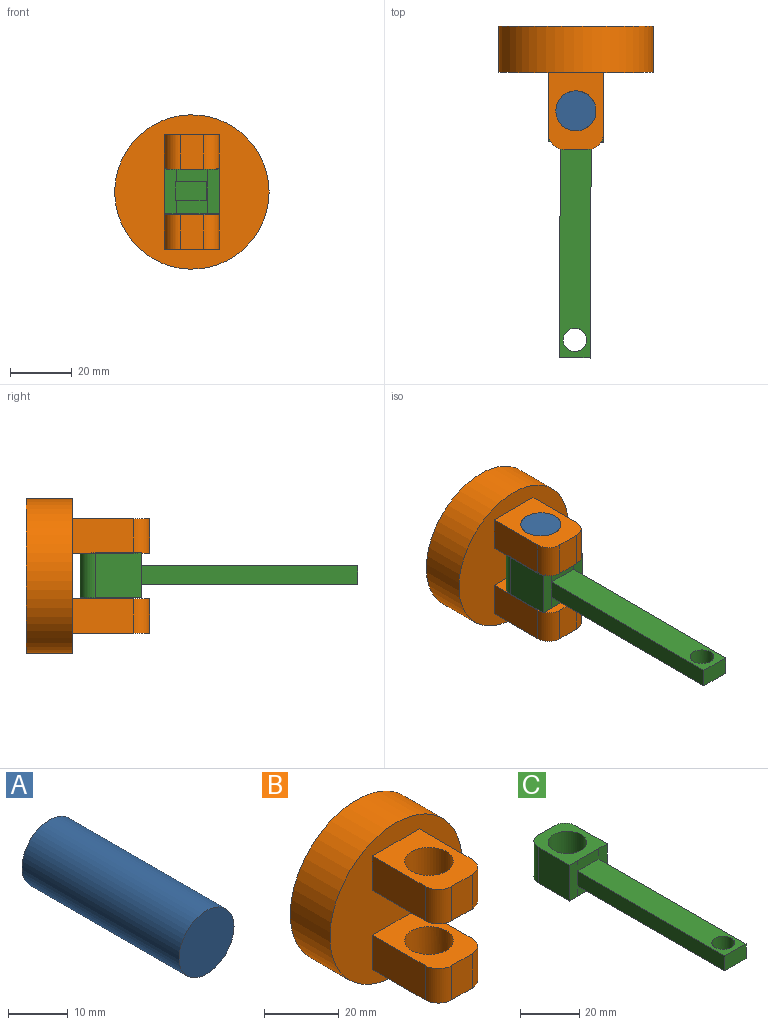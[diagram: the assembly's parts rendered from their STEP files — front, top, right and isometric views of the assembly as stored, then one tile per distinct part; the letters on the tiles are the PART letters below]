
ASSEMBLY  parts=3 mates=2
PART A: 3 faces, bbox 13x37.2x13 mm
  f0: cylinder r=6.5mm len=37.21mm, axis (0,1,0), area 1519.7mm2, adj f1,f2
  f1: plane 13x13mm, normal (0,-1,0), area 132.7mm2, adj f0
  f2: plane 13x13mm, normal (0,1,0), area 132.7mm2, adj f0
PART B: 19 faces, bbox 50x40x50 mm
  f0: plane 19.92x11.26mm, normal (-1,0,0), area 224.3mm2, adj f5,f8,f14,f16
  f1: plane 19.92x11.26mm, normal (1,0,0), area 224.3mm2, adj f5,f8,f14,f15
  f2: plane 11.26x7.62mm, normal (0,-1,0), area 85.9mm2, adj f8,f14,f15,f16
  f3: cylinder r=6.5mm len=13mm, axis (0,0,-1), area 459.9mm2, adj f8,f14
  f4: cylinder r=25mm len=50mm, axis (0,1,0), area 2356.2mm2, adj f5,f6
  f5: plane 50x50mm, normal (0,-1,0), area 1563mm2, adj f0,f1,f4,f7,f8,f9,f10,f13
  f6: plane 50x50mm, normal (0,1,0), area 1963.5mm2, adj f4
  f7: plane 19.92x11.26mm, normal (-1,0,0), area 224.3mm2, adj f5,f10,f13,f18
  f8: plane 25x17.78mm, normal (0,0,-1), area 300.8mm2, adj f0,f1,f2,f3,f5,f15,f16
  f9: plane 19.92x11.26mm, normal (1,0,0), area 224.3mm2, adj f5,f10,f13,f17
  f10: plane 25x17.78mm, normal (0,0,1), area 300.8mm2, adj f5,f7,f9,f11,f12,f17,f18
  f11: plane 11.26x7.62mm, normal (0,-1,0), area 85.9mm2, adj f10,f13,f17,f18
  f12: cylinder r=6.5mm len=13mm, axis (0,0,-1), area 459.9mm2, adj f10,f13
  f13: plane 25x17.78mm, normal (0,0,-1), area 300.8mm2, adj f5,f7,f9,f11,f12,f17,f18
  f14: plane 25x17.78mm, normal (0,0,1), area 300.8mm2, adj f0,f1,f2,f3,f5,f15,f16
  f15: cylinder r=5.08mm len=11.26mm, axis (0,0,-1), area 89.9mm2, adj f1,f2,f8,f14
  f16: cylinder r=5.08mm len=11.26mm, axis (0,0,1), area 89.9mm2, adj f0,f2,f8,f14
  f17: cylinder r=5.08mm len=11.26mm, axis (0,0,-1), area 89.9mm2, adj f9,f10,f11,f13
  f18: cylinder r=5.08mm len=11.26mm, axis (0,0,1), area 89.9mm2, adj f7,f10,f11,f13
PART C: 18 faces, bbox 17.8x90x14.7 mm
  f0: plane 70x6.11mm, normal (-1,0,0), area 427.9mm2, adj f1,f4,f10,f12
  f1: plane 10x6.11mm, normal (0,-1,0), area 61.1mm2, adj f0,f2,f10,f12
  f2: plane 70x6.11mm, normal (1,0,0), area 427.9mm2, adj f1,f5,f10,f12
  f3: plane 14.92x14.69mm, normal (-1,0,0), area 219.1mm2, adj f4,f8,f9,f16
  f4: plane 14.69x3.9mm, normal (0,-1,0), area 57.3mm2, adj f0,f3,f8,f9,f11,f13
  f5: plane 14.69x3.89mm, normal (0,-1,0), area 57.1mm2, adj f2,f6,f8,f9,f11,f13
  f6: plane 14.92x14.69mm, normal (1,0,0), area 219.1mm2, adj f5,f8,f9,f15
  f7: plane 14.69x7.62mm, normal (0,1,0), area 112mm2, adj f8,f9,f15,f16
  f8: plane 20x17.78mm, normal (0,0,1), area 211.9mm2, adj f3,f4,f5,f6,f7,f13,f14,f15
  f9: plane 20x17.78mm, normal (0,0,-1), area 211.9mm2, adj f3,f4,f5,f6,f7,f11,f14,f15
  f10: plane 70x10mm, normal (0,0,-1), area 654.4mm2, adj f0,f1,f2,f11,f17
  f11: plane 10x4.29mm, normal (0,-1,0), area 42.9mm2, adj f4,f5,f9,f10
  f12: plane 70x10mm, normal (0,0,1), area 654.4mm2, adj f0,f1,f2,f13,f17
  f13: plane 10x4.29mm, normal (0,-1,0), area 42.9mm2, adj f4,f5,f8,f12
  f14: cylinder r=6.5mm len=14.69mm, axis (0,0,1), area 599.8mm2, adj f8,f9
  f15: cylinder r=5.08mm len=14.69mm, axis (0,0,1), area 117.2mm2, adj f6,f7,f8,f9
  f16: cylinder r=5.08mm len=14.69mm, axis (0,0,-1), area 117.2mm2, adj f3,f7,f8,f9
  f17: cylinder r=3.81mm len=7.62mm, axis (0,0,1), area 146.3mm2, adj f10,f12
PLACE A rot(axis=(0,-0.71,0.71),179.8deg) t=(-32.95,39.4,-15.61)mm
PLACE B t=(-32.95,66.9,3)mm fixed
PLACE C rot(axis=(0,1,0),180deg) t=(-33.16,-5.6,10.62)mm
MATE revolute A.f0 <-> B.f3  axis (0,0,1) through (-32.95,39.4,21.6)mm
MATE fastened A.f0 <-> C.f14  axis (0,0,-1) through (-32.95,39.4,3)mm
